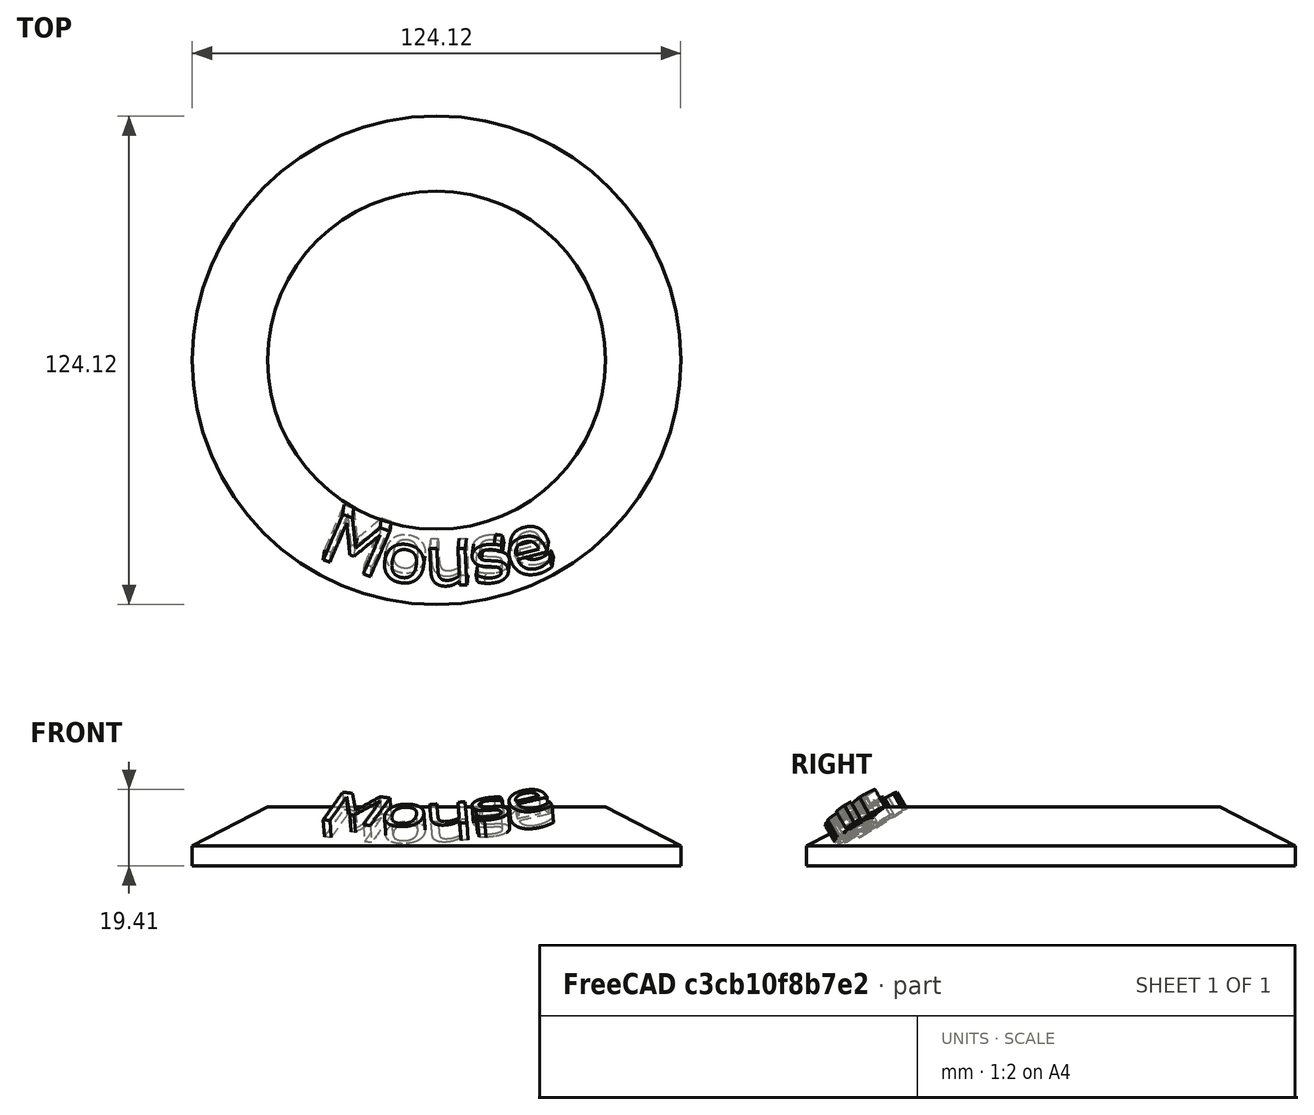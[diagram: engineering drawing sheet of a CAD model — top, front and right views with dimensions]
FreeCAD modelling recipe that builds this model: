
FCSTD DOCUMENT  (FreeCAD 0.19R24291 (Git))
Label: individual-ferret-with-base 2
License: All rights reserved
LicenseURL: http://en.wikipedia.org/wiki/All_rights_reserved
objects: Part::Feature×7, Part::Extrusion×7, Part::Cut×2, Part::MultiFuse×1, Mesh::Feature×1, Sketcher::SketchObject×1, PartDesign::Revolution×1, PartDesign::Body×1
note: 21 computed .brp shape members not serialized (recipe doc carries the construction recipe); baked Part::Feature solids carry a one-line shape summary decoded from their .brp

FEATURE [Part::Feature] Face
  shape: bbox 15.91 x 14.55 x 2e-07 mm, 1 faces, 0 solids (baked)
FEATURE [Part::Feature] Face001
  shape: bbox 11.7 x 10.66 x 2e-07 mm, 1 faces, 0 solids (baked)
FEATURE [Part::Feature] Face002
  shape: bbox 8.382 x 6.942 x 2e-07 mm, 1 faces, 0 solids (baked)
FEATURE [Part::Feature] Face003
  shape: bbox 12.99 x 13.22 x 2e-07 mm, 1 faces, 0 solids (baked)
FEATURE [Part::Feature] Face004
  shape: bbox 12.48 x 10.91 x 2e-07 mm, 1 faces, 0 solids (baked)
FEATURE [Part::Feature] Face005
  shape: bbox 11.17 x 12.16 x 2e-07 mm, 1 faces, 0 solids (baked)
FEATURE [Part::Feature] Face006
  shape: bbox 5.504 x 5.148 x 2e-07 mm, 1 faces, 0 solids (baked)
FEATURE [Part::Extrusion] Extrude
  Base = -> Face
  Dir = (0,0,-1)
  DirMode = 0
  FaceMakerClass = Part::FaceMakerBullseye
  LengthFwd = 5
  LengthRev = 0
  Solid = true
  Symmetric = false
FEATURE [Part::Extrusion] Extrude001
  Base = -> Face001
  Dir = (0,0,-1)
  DirMode = 0
  FaceMakerClass = Part::FaceMakerBullseye
  LengthFwd = 5
  LengthRev = 0
  Solid = true
  Symmetric = false
FEATURE [Part::Extrusion] Extrude002
  Base = -> Face002
  Dir = (0,0,-1)
  DirMode = 0
  FaceMakerClass = Part::FaceMakerBullseye
  LengthFwd = 5
  LengthRev = 0
  Solid = true
  Symmetric = false
FEATURE [Part::Extrusion] Extrude003
  Base = -> Face003
  Dir = (0,0,-1)
  DirMode = 0
  FaceMakerClass = Part::FaceMakerBullseye
  LengthFwd = 5
  LengthRev = 0
  Solid = true
  Symmetric = false
FEATURE [Part::Extrusion] Extrude004
  Base = -> Face004
  Dir = (0,0,-1)
  DirMode = 0
  FaceMakerClass = Part::FaceMakerBullseye
  LengthFwd = 5
  LengthRev = 0
  Solid = true
  Symmetric = false
FEATURE [Part::Extrusion] Extrude005
  Base = -> Face005
  Dir = (0,0,-1)
  DirMode = 0
  FaceMakerClass = Part::FaceMakerBullseye
  LengthFwd = 5
  LengthRev = 0
  Solid = true
  Symmetric = false
FEATURE [Part::Extrusion] Extrude006
  Base = -> Face006
  Dir = (0,0,-1)
  DirMode = 0
  FaceMakerClass = Part::FaceMakerBullseye
  LengthFwd = 5
  LengthRev = 0
  Solid = true
  Symmetric = false
FEATURE [Part::Cut] Cut
  Base = -> Extrude001
  Tool = -> Extrude002
FEATURE [Part::Cut] Cut001
  Base = -> Extrude005
  Tool = -> Extrude006
FEATURE [Part::MultiFuse] Fusion
  Placement = pos=(-114.69,-85.4587,-30.0239) rot=(0.364924,-0.290822,0.884451;1.17807rad)
  Shapes = -> [Extrude,Extrude003,Extrude004,Cut,Cut001]
FEATURE [Mesh::Feature] Ferret002  label="Ferret"
  Placement = pos=(-124.357,-109.694,-3.28686) rot=(0,0,1;0rad)
FEATURE [Sketcher::SketchObject] Sketch
  FullyConstrained = false
  MapMode = 5
  Placement = pos=(0,0,0) rot=(1,0,0;1.5708rad)
  Support = -> [XZ_Plane001]
  sketch-geometry (5):
    g0: LineSegment StartX=0 StartY=0 StartZ=0 EndX=-42.9267 EndY=0 EndZ=0
    g1: LineSegment StartX=-42.9267 StartY=0 StartZ=0 EndX=-62.0627 EndY=-9.87524 EndZ=0
    g2: LineSegment StartX=-62.0627 StartY=-9.87524 StartZ=0 EndX=-62.0627 EndY=-14.9492 EndZ=0
    g3: LineSegment StartX=-62.0627 StartY=-14.9492 StartZ=0 EndX=0 EndY=-14.9492 EndZ=0
    g4: LineSegment StartX=0 StartY=-14.9492 StartZ=0 EndX=0 EndY=0 EndZ=0
  constraints (10):
    c: Coincident(g-1,g0)
    c: PointOnObject(g0,g-1)
    c: Coincident(g0,g1)
    c: Coincident(g1,g2)
    c: Vertical(g2)
    c: Coincident(g2,g3)
    c: PointOnObject(g3,g-2)
    c: Horizontal(g3)
    c: Coincident(g3,g4)
    c: Coincident(g4,g0)
FEATURE [PartDesign::Revolution] Revolution
  Angle = 360
  Axis = (0,-2e-16,1)
  Base = (0,0,0)
  Placement = pos=(0,0,0) rot=(1,0,0;1.5708rad)
  Profile = -> Sketch
  ReferenceAxis = -> Sketch [V_Axis]
FEATURE [PartDesign::Body] Body001
  Group = -> [Sketch,Revolution]
  Origin = -> Origin001
  Tip = -> Revolution
